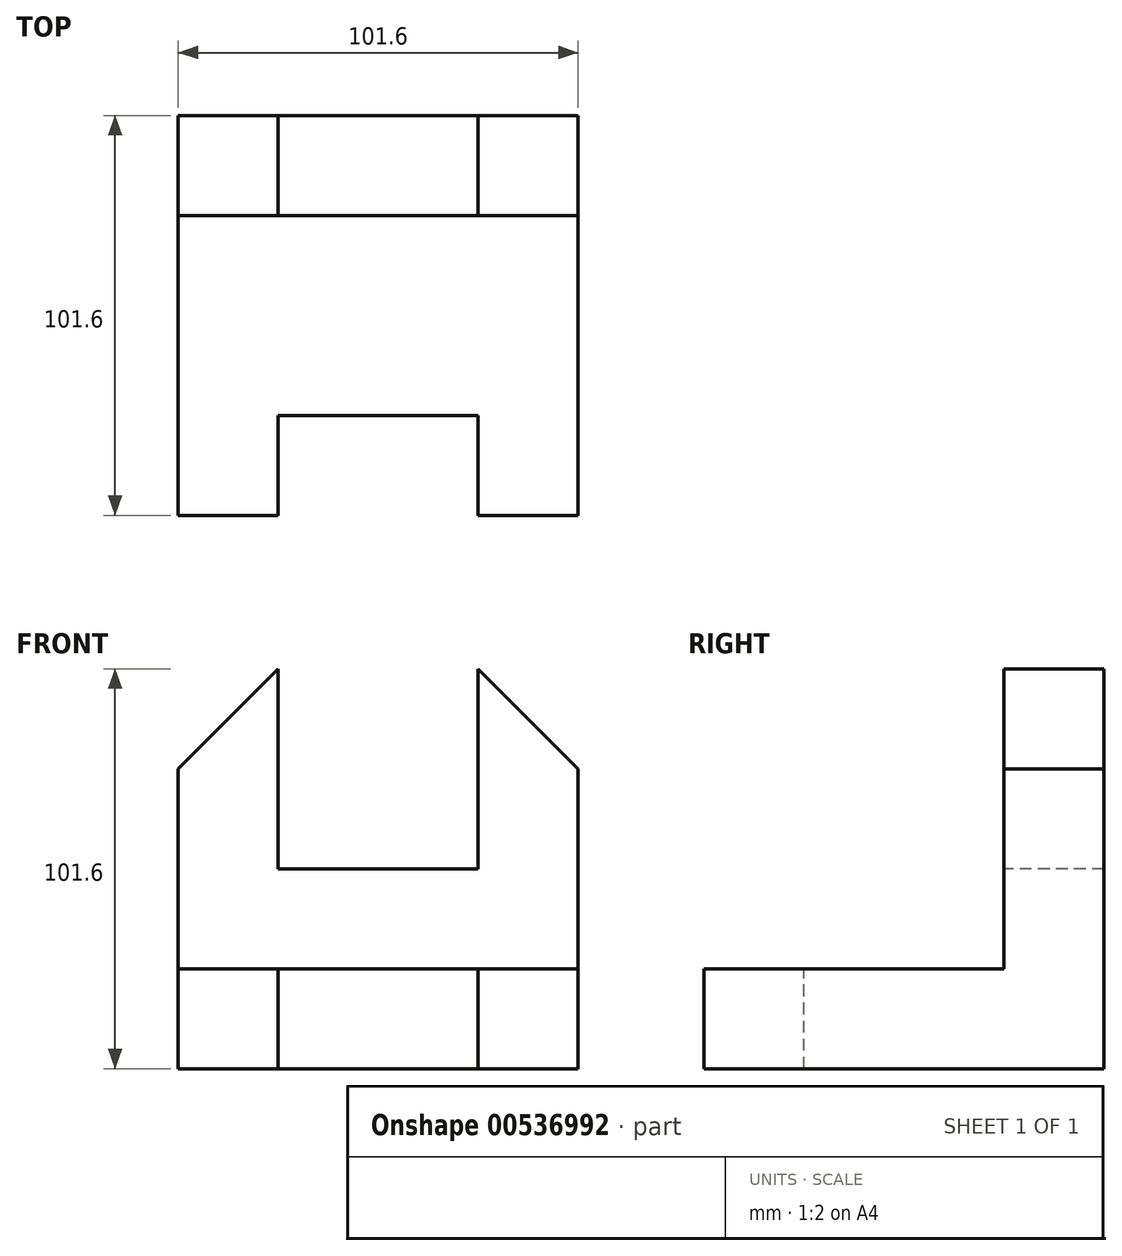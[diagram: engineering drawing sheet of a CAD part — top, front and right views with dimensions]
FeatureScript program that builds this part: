
annotation { "Feature Type Name" : "Feature", "Feature Type Description" : "" }
export const myFeature = defineFeature(function(context is Context, id is Id, definition is map)
    precondition{}
    {
        {
            var Q0;
            Q0=qCreatedBy(makeId("Top.planeOp"),FACE);
            var sketch = newSketch(context, id + "F0", { "sketchPlane" : qUnion([Q0])});
            skLineSegment(sketch, "E0.bottom", {"start": v(0, 0) * mm, "end": v(-101.6, 0) * mm});
            skLineSegment(sketch, "E0.top", {"start": v(0, -101.6) * mm, "end": v(-101.6, -101.6) * mm});
            skLineSegment(sketch, "E0.left", {"start": v(0, 0) * mm, "end": v(0, -101.6) * mm});
            skLineSegment(sketch, "E0.right", {"start": v(-101.6, 0) * mm, "end": v(-101.6, -101.6) * mm});
            skSolve(sketch);
        }
        {
            var Q0;
            Q0=makeQuery(id+"F0.imprint","IMPRINT",FACE,{"disambiguationData":[TD([[makeQuery(id+"F0.imprint","IMPRINT",EDGE,{"derivedFrom":sQuery(id+"F0.wireOp",EDGE,"E0.bottom")}),1.0]])]});
            extrude(context, id + "F1", {"entities" : qUnion([Q0]), "depth" : 101.6 * mm, "offsetDistance" : 25.4 * mm});
        }
        {
            var Q0;
            Q0=makeQuery(id+"F1.opExtrude","SWEPT_FACE",FACE,{"disambiguationData":[OSD([sQuery(id+"F0.wireOp",EDGE,"E0.left")])]});
            var sketch = newSketch(context, id + "F2", { "sketchPlane" : qUnion([Q0])});
            skLineSegment(sketch, "E1", {"start": v(-101.6, 0) * mm, "end": v(-101.6, 25.4) * mm});
            skLineSegment(sketch, "E2", {"start": v(-101.6, 25.4) * mm, "end": v(-25.4, 25.4) * mm});
            skLineSegment(sketch, "E3", {"start": v(-25.4, 25.4) * mm, "end": v(-25.4, 101.6) * mm});
            skSolve(sketch);
        }
        {
            var Q0;
            {var subQ0=sQuery(id+"F2.wireOp",EDGE,"E2");Q0=makeQuery(id+"F2.imprint","IMPRINT",FACE,{"disambiguationData":[TD([[makeQuery(id+"F2.imprint","IMPRINT",EDGE,{"derivedFrom":subQ0}),1.0]])]});}
            extrude(context, id + "F3", {"entities" : qUnion([Q0]), "operationType" : NewBodyOperationType.REMOVE, "oppositeDirection" : true, "depth" : 107.19 * mm, "offsetDistance" : 25.4 * mm});
        }
        {
            var Q0;
            Q0=makeQuery(id+"F3.boolean.opBoolean","COPY",FACE,{"derivedFrom":makeQuery(id+"F3.opExtrude","SWEPT_FACE",FACE,{"disambiguationData":[OSD([sQuery(id+"F2.wireOp",EDGE,"E3")])]})});
            var sketch = newSketch(context, id + "F4", { "sketchPlane" : qUnion([Q0])});
            skLineSegment(sketch, "E4", {"start": v(-101.6, 101.6) * mm, "end": v(-76.2, 101.6) * mm});
            skLineSegment(sketch, "E5", {"start": v(-76.2, 101.6) * mm, "end": v(-76.2, 50.8) * mm});
            skLineSegment(sketch, "E6", {"start": v(-76.2, 50.8) * mm, "end": v(-25.4, 50.8) * mm});
            skLineSegment(sketch, "E7", {"start": v(-25.4, 50.8) * mm, "end": v(-25.4, 101.6) * mm});
            skLineSegment(sketch, "E8", {"start": v(-25.4, 101.6) * mm, "end": v(0, 76.2) * mm});
            skLineSegment(sketch, "E9", {"start": v(-76.2, 101.6) * mm, "end": v(-101.6, 76.2) * mm});
            skLineSegment(sketch, "E10", {"start": v(-101.6, 76.2) * mm, "end": v(-101.6, 101.6) * mm});
            skLineSegment(sketch, "E11", {"start": v(-25.4, 101.6) * mm, "end": v(0, 101.6) * mm});
            skLineSegment(sketch, "E12", {"start": v(0, 101.6) * mm, "end": v(0, 76.2) * mm});
            skSolve(sketch);
        }
        {
            var Q0;
            {var subQ0=sQuery(id+"F4.wireOp",EDGE,"E5");Q0=makeQuery(id+"F4.imprint","IMPRINT",FACE,{"disambiguationData":[TD([[makeQuery(id+"F4.imprint","IMPRINT",EDGE,{"derivedFrom":subQ0}),1.0]])]});}
            var Q1;
            Q1=makeQuery(id+"F4.imprint","IMPRINT",FACE,{"disambiguationData":[TD([[makeQuery(id+"F4.imprint","IMPRINT",EDGE,{"derivedFrom":sQuery(id+"F4.wireOp",EDGE,"E8")}),1.0]])]});
            var Q2;
            Q2=makeQuery(id+"F4.imprint","IMPRINT",FACE,{"disambiguationData":[TD([[makeQuery(id+"F4.imprint","IMPRINT",EDGE,{"derivedFrom":sQuery(id+"F4.wireOp",EDGE,"E4")}),-1.0]])]});
            extrude(context, id + "F5", {"entities" : qUnion([Q0, Q1, Q2]), "operationType" : NewBodyOperationType.REMOVE, "oppositeDirection" : true, "depth" : 30.48 * mm, "offsetDistance" : 25.4 * mm});
        }
        {
            var Q0;
            Q0=makeQuery(id+"F3.boolean.opBoolean","COPY",FACE,{"derivedFrom":makeQuery(id+"F3.opExtrude","SWEPT_FACE",FACE,{"disambiguationData":[OSD([sQuery(id+"F2.wireOp",EDGE,"E2")])]})});
            var sketch = newSketch(context, id + "F6", { "sketchPlane" : qUnion([Q0])});
            skLineSegment(sketch, "E13", {"start": v(-101.6, -101.6) * mm, "end": v(-76.2, -101.6) * mm});
            skLineSegment(sketch, "E14", {"start": v(-76.2, -101.6) * mm, "end": v(-76.2, -76.2) * mm});
            skLineSegment(sketch, "E15", {"start": v(-76.2, -76.2) * mm, "end": v(-25.4, -76.2) * mm});
            skLineSegment(sketch, "E16", {"start": v(-25.4, -76.2) * mm, "end": v(-25.4, -101.6) * mm});
            skSolve(sketch);
        }
        {
            var Q0;
            {var subQ0=sQuery(id+"F6.wireOp",EDGE,"E14");Q0=makeQuery(id+"F6.imprint","IMPRINT",FACE,{"disambiguationData":[TD([[makeQuery(id+"F6.imprint","IMPRINT",EDGE,{"derivedFrom":subQ0}),-1.0]])]});}
            extrude(context, id + "F7", {"entities" : qUnion([Q0]), "operationType" : NewBodyOperationType.REMOVE, "oppositeDirection" : true, "depth" : 40.13 * mm, "offsetDistance" : 25.4 * mm});
        }
    });
